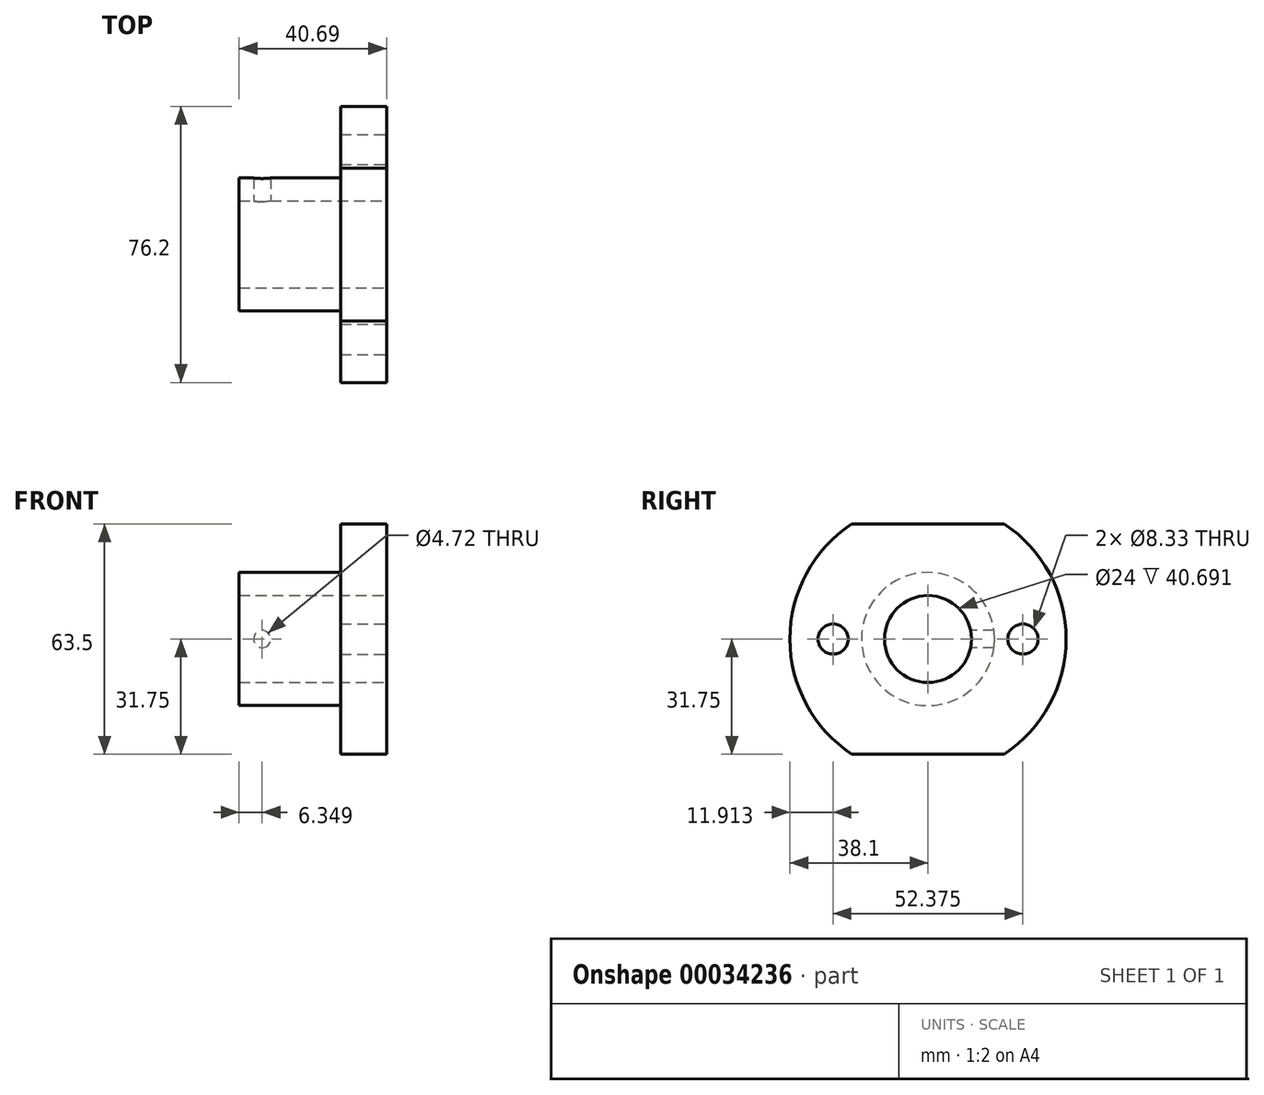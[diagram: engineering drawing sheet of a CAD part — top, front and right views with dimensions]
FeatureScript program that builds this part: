
annotation { "Feature Type Name" : "Feature", "Feature Type Description" : "" }
export const myFeature = defineFeature(function(context is Context, id is Id, definition is map)
    precondition{}
    {
        {
            var Q0;
            Q0=qCreatedBy(makeId("Right.planeOp"),FACE);
            var sketch = newSketch(context, id + "F0", { "sketchPlane" : qUnion([Q0])});
            skArc(sketch, "E0", {"start": v(-21.06, 31.75) * mm, "mid": v(-38.1, 0) * mm, "end": v(-21.06, -31.75) * mm});
            skPoint(sketch, "E1", {"position": v(26.19, 0) * mm});
            skPoint(sketch, "E2.1.0", {"position": v(-26.19, 0) * mm});
            skLineSegment(sketch, "E3", {"start": v(-21.06, 31.75) * mm, "end": v(21.06, 31.75) * mm});
            skLineSegment(sketch, "E4.1.0", {"start": v(21.06, -31.75) * mm, "end": v(-21.06, -31.75) * mm});
            skArc(sketch, "E5.trimOffspring", {"start": v(21.06, -31.75) * mm, "mid": v(38.1, 0) * mm, "end": v(21.06, 31.75) * mm});
            skPoint(sketch, "E6.orphan", {"position": v(-50.66, -31.75) * mm});
            skPoint(sketch, "E7.orphan", {"position": v(41.85, -31.75) * mm});
            skPoint(sketch, "E8.orphan", {"position": v(50.66, 31.75) * mm});
            skPoint(sketch, "E9.orphan", {"position": v(-41.85, 31.75) * mm});
            skSolve(sketch);
        }
        {
            var Q0;
            Q0 = qSketchRegion(id + "F0", true);
            extrude(context, id + "F1", {"entities" : qUnion([Q0]), "oppositeDirection" : true, "depth" : 12.7 * mm});
        }
        {
            var Q0;
            Q0=makeQuery(id+"F1.opExtrude","CAP_FACE",FACE,{"disambiguationData":[OSD([sQuery(id+"F0.wireOp",EDGE,"E0"),sQuery(id+"F0.wireOp",EDGE,"E3"),sQuery(id+"F0.wireOp",EDGE,"E4.1.0"),sQuery(id+"F0.wireOp",EDGE,"E5.trimOffspring")])],"isStart":false});
            var sketch = newSketch(context, id + "F2", { "sketchPlane" : qUnion([Q0])});
            skCircle(sketch, "E10", {"center": v(0, 0) * mm, "radius": 18.35 * mm});
            skSolve(sketch);
        }
        {
            var Q0;
            Q0 = qSketchRegion(id + "F2", true);
            extrude(context, id + "F3", {"entities" : qUnion([Q0]), "operationType" : NewBodyOperationType.ADD, "depth" : 28 * mm});
        }
        {
            var Q0;
            Q0=makeQuery(id+"F1.opExtrude","CAP_FACE",FACE,{"disambiguationData":[OSD([sQuery(id+"F0.wireOp",EDGE,"E0"),sQuery(id+"F0.wireOp",EDGE,"E3"),sQuery(id+"F0.wireOp",EDGE,"E4.1.0"),sQuery(id+"F0.wireOp",EDGE,"E5.trimOffspring")])],"isStart":true});
            var sketch = newSketch(context, id + "F4", { "sketchPlane" : qUnion([Q0])});
            skCircle(sketch, "E11", {"center": v(0, 0) * mm, "radius": 12 * mm});
            skSolve(sketch);
        }
        {
            var Q0;
            Q0 = qSketchRegion(id + "F4", true);
            extrude(context, id + "F5", {"entities" : qUnion([Q0]), "operationType" : NewBodyOperationType.REMOVE, "endBound" : BoundingType.THROUGH_ALL, "oppositeDirection" : true, "depth" : 25.4 * mm});
        }
        {
            var Q0;
            Q0=sQuery(id+"F0.wireOp",VERTEX,"E1");
            var Q1;
            Q1=sQuery(id+"F0.wireOp",VERTEX,"E2.1.0");
            var Q2;
            Q2=makeQuery(id+"F1.opExtrude","SWEPT_BODY",BODY,{"disambiguationData":[OSD([sQuery(id+"F0.wireOp",EDGE,"E0"),sQuery(id+"F0.wireOp",EDGE,"E3"),sQuery(id+"F0.wireOp",EDGE,"E4.1.0"),sQuery(id+"F0.wireOp",EDGE,"E5.trimOffspring")])]});
            hole(context, id + "F6", {"style" : HoleStyle.SIMPLE, "holeDiameter" : 8.33 * mm, "endStyle" : HoleEndStyle.THROUGH, "locations" : qUnion([Q0, Q1]), "scope" : qUnion([Q2])});
        }
        {
            var Q0;
            Q0=qCreatedBy(makeId("Front.planeOp"),FACE);
            var sketch = newSketch(context, id + "F7", { "sketchPlane" : qUnion([Q0])});
            skCircle(sketch, "E12", {"center": v(-34.34, 0) * mm, "radius": 2.36 * mm});
            skSolve(sketch);
        }
        {
            var Q0;
            Q0 = qSketchRegion(id + "F7", true);
            extrude(context, id + "F8", {"entities" : qUnion([Q0]), "operationType" : NewBodyOperationType.REMOVE, "oppositeDirection" : true, "depth" : 25.4 * mm});
        }
    });
